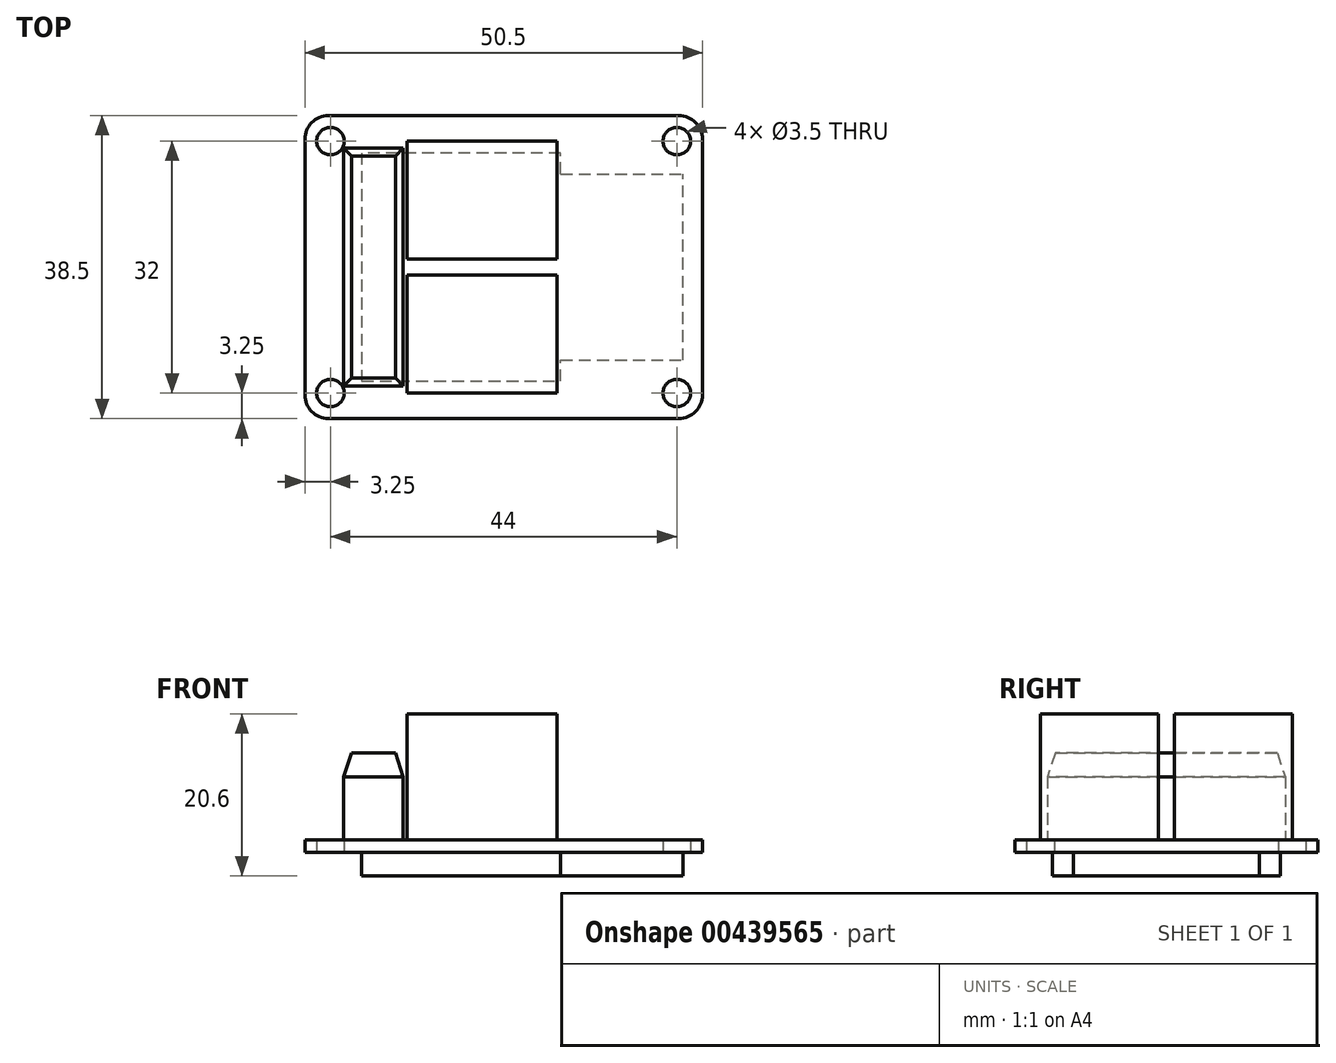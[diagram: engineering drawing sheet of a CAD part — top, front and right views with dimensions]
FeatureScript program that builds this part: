
annotation { "Feature Type Name" : "Feature", "Feature Type Description" : "" }
export const myFeature = defineFeature(function(context is Context, id is Id, definition is map)
    precondition{}
    {
        {
            var Q0;
            Q0=qCreatedBy(makeId("Top.planeOp"),FACE);
            var sketch = newSketch(context, id + "F0", { "sketchPlane" : qUnion([Q0])});
            skLineSegment(sketch, "E0.bottom", {"start": v(-28, -60) * mm, "end": v(22.5, -60) * mm});
            skLineSegment(sketch, "E0.top", {"start": v(-28, -98.5) * mm, "end": v(22.5, -98.5) * mm});
            skLineSegment(sketch, "E0.left", {"start": v(-28, -60) * mm, "end": v(-28, -98.5) * mm});
            skLineSegment(sketch, "E0.right", {"start": v(22.5, -60) * mm, "end": v(22.5, -98.5) * mm});
            skCircle(sketch, "E1", {"center": v(-24.75, -63.25) * mm, "radius": 1.75 * mm});
            skCircle(sketch, "E2.0.1.0", {"center": v(-24.75, -95.25) * mm, "radius": 1.75 * mm});
            skCircle(sketch, "E2.1.0.0", {"center": v(19.25, -63.25) * mm, "radius": 1.75 * mm});
            skCircle(sketch, "E2.1.1.0", {"center": v(19.25, -95.25) * mm, "radius": 1.75 * mm});
            skLineSegment(sketch, "E2.direction1", {"start": v(-24.75, -63.25) * mm, "end": v(19.25, -63.25) * mm, "construction": true});
            skLineSegment(sketch, "E2.direction2", {"start": v(-24.75, -63.25) * mm, "end": v(-24.75, -95.25) * mm, "construction": true});
            skSolve(sketch);
        }
        {
            var Q0;
            Q0=makeQuery(id+"F0.imprint","IMPRINT",FACE,{"disambiguationData":[TD([[makeQuery(id+"F0.imprint","IMPRINT",EDGE,{"derivedFrom":sQuery(id+"F0.wireOp",EDGE,"E0.bottom")}),-1.0]])]});
            extrude(context, id + "F1", {"entities" : qUnion([Q0]), "depth" : 4.6 * mm, "hasSecondDirection" : true, "secondDirectionOppositeDirection" : false, "secondDirectionDepth" : 3 * mm});
        }
        {
            var Q0;
            Q0=makeQuery(id+"F1.opExtrude","SWEPT_EDGE",EDGE,{"disambiguationData":[OSD([sQuery(id+"F0.wireOp",EDGE,"E0.top"),sQuery(id+"F0.wireOp",EDGE,"E0.right")])]});
            var Q1;
            Q1=makeQuery(id+"F1.opExtrude","SWEPT_EDGE",EDGE,{"disambiguationData":[OSD([sQuery(id+"F0.wireOp",EDGE,"E0.bottom"),sQuery(id+"F0.wireOp",EDGE,"E0.right")])]});
            var Q2;
            Q2=makeQuery(id+"F1.opExtrude","SWEPT_EDGE",EDGE,{"disambiguationData":[OSD([sQuery(id+"F0.wireOp",EDGE,"E0.bottom"),sQuery(id+"F0.wireOp",EDGE,"E0.left")])]});
            var Q3;
            Q3=makeQuery(id+"F1.opExtrude","SWEPT_EDGE",EDGE,{"disambiguationData":[OSD([sQuery(id+"F0.wireOp",EDGE,"E0.top"),sQuery(id+"F0.wireOp",EDGE,"E0.left")])]});
            fillet(context, id + "F2", {"entities" : qUnion([Q0, Q1, Q2, Q3]), "radius" : 3 * mm, "tangentPropagation" : true, "allowEdgeOverflow" : false});
        }
        {
            var Q0;
            Q0=makeQuery(id+"F1.opExtrude","CAP_FACE",FACE,{"disambiguationData":[OSD([sQuery(id+"F0.wireOp",EDGE,"E0.bottom"),sQuery(id+"F0.wireOp",EDGE,"E0.top"),sQuery(id+"F0.wireOp",EDGE,"E0.left"),sQuery(id+"F0.wireOp",EDGE,"E0.right"),sQuery(id+"F0.wireOp",EDGE,"E1"),sQuery(id+"F0.wireOp",EDGE,"E2.0.1.0"),sQuery(id+"F0.wireOp",EDGE,"E2.1.0.0"),sQuery(id+"F0.wireOp",EDGE,"E2.1.1.0")])],"isStart":true});
            var sketch = newSketch(context, id + "F3", { "sketchPlane" : qUnion([Q0])});
            skLineSegment(sketch, "E3.0.0", {"start": v(19.5, 98.5) * mm, "end": v(-25, 98.5) * mm, "construction": true});
            skArc(sketch, "E3.0.1", {"start": v(-25, 98.5) * mm, "mid": v(-27.12, 97.62) * mm, "end": v(-28, 95.5) * mm, "construction": true});
            skLineSegment(sketch, "E3.0.2", {"start": v(-28, 95.5) * mm, "end": v(-28, 63) * mm, "construction": true});
            skArc(sketch, "E3.0.3", {"start": v(-28, 63) * mm, "mid": v(-27.12, 60.88) * mm, "end": v(-25, 60) * mm, "construction": true});
            skLineSegment(sketch, "E3.0.4", {"start": v(-25, 60) * mm, "end": v(19.5, 60) * mm, "construction": true});
            skArc(sketch, "E3.0.5", {"start": v(19.5, 60) * mm, "mid": v(21.62, 60.88) * mm, "end": v(22.5, 63) * mm, "construction": true});
            skLineSegment(sketch, "E3.0.6", {"start": v(22.5, 63) * mm, "end": v(22.5, 95.5) * mm, "construction": true});
            skArc(sketch, "E3.0.7", {"start": v(22.5, 95.5) * mm, "mid": v(21.62, 97.62) * mm, "end": v(19.5, 98.5) * mm, "construction": true});
            skCircle(sketch, "E4.0", {"center": v(-24.75, 95.25) * mm, "radius": 1.75 * mm, "construction": true});
            skCircle(sketch, "E5.0", {"center": v(19.25, 95.25) * mm, "radius": 1.75 * mm, "construction": true});
            skCircle(sketch, "E6.0", {"center": v(19.25, 63.25) * mm, "radius": 1.75 * mm, "construction": true});
            skCircle(sketch, "E7.0", {"center": v(-24.75, 63.25) * mm, "radius": 1.75 * mm, "construction": true});
            skLineSegment(sketch, "E8", {"start": v(-20.77, 64.75) * mm, "end": v(-20.77, 93.75) * mm});
            skLineSegment(sketch, "E9", {"start": v(-20.77, 93.75) * mm, "end": v(4.5, 93.75) * mm});
            skLineSegment(sketch, "E10", {"start": v(4.5, 93.75) * mm, "end": v(4.5, 64.75) * mm});
            skLineSegment(sketch, "E11", {"start": v(4.5, 64.75) * mm, "end": v(-20.77, 64.75) * mm});
            skPoint(sketch, "E12.orphan", {"position": v(19.25, 93.75) * mm});
            skLineSegment(sketch, "E13.bottom", {"start": v(4.5, 91.07) * mm, "end": v(20, 91.07) * mm});
            skLineSegment(sketch, "E13.top", {"start": v(4.5, 67.43) * mm, "end": v(20, 67.43) * mm});
            skLineSegment(sketch, "E13.left", {"start": v(4.5, 91.07) * mm, "end": v(4.5, 67.43) * mm});
            skLineSegment(sketch, "E13.right", {"start": v(20, 91.07) * mm, "end": v(20, 67.43) * mm});
            skSolve(sketch);
        }
        {
            var Q0;
            Q0=makeQuery(id+"F3.imprint","IMPRINT",FACE,{"disambiguationData":[TD([[makeQuery(id+"F3.imprint","IMPRINT",EDGE,{"derivedFrom":sQuery(id+"F3.wireOp",EDGE,"E8")}),-1.0]])]});
            var Q1;
            Q1=makeQuery(id+"F3.imprint","IMPRINT",FACE,{"disambiguationData":[TD([[makeQuery(id+"F3.imprint","IMPRINT",EDGE,{"derivedFrom":sQuery(id+"F3.wireOp",EDGE,"E13.bottom")}),-1.0]])]});
            extrude(context, id + "F4", {"entities" : qUnion([Q0, Q1]), "operationType" : NewBodyOperationType.ADD, "depth" : 3 * mm});
        }
        {
            var Q0;
            Q0=makeQuery(id+"F1.opExtrude","CAP_FACE",FACE,{"disambiguationData":[OSD([sQuery(id+"F0.wireOp",EDGE,"E0.bottom"),sQuery(id+"F0.wireOp",EDGE,"E0.top"),sQuery(id+"F0.wireOp",EDGE,"E0.left"),sQuery(id+"F0.wireOp",EDGE,"E0.right"),sQuery(id+"F0.wireOp",EDGE,"E1"),sQuery(id+"F0.wireOp",EDGE,"E2.0.1.0"),sQuery(id+"F0.wireOp",EDGE,"E2.1.0.0"),sQuery(id+"F0.wireOp",EDGE,"E2.1.1.0")])],"isStart":false});
            var sketch = newSketch(context, id + "F5", { "sketchPlane" : qUnion([Q0])});
            skLineSegment(sketch, "E14.0.0", {"start": v(-28, -63) * mm, "end": v(-28, -95.5) * mm, "construction": true});
            skArc(sketch, "E14.0.1", {"start": v(-28, -95.5) * mm, "mid": v(-27.12, -97.62) * mm, "end": v(-25, -98.5) * mm, "construction": true});
            skLineSegment(sketch, "E14.0.2", {"start": v(-25, -98.5) * mm, "end": v(19.5, -98.5) * mm, "construction": true});
            skArc(sketch, "E14.0.3", {"start": v(19.5, -98.5) * mm, "mid": v(21.62, -97.62) * mm, "end": v(22.5, -95.5) * mm, "construction": true});
            skLineSegment(sketch, "E14.0.4", {"start": v(22.5, -95.5) * mm, "end": v(22.5, -63) * mm, "construction": true});
            skArc(sketch, "E14.0.5", {"start": v(22.5, -63) * mm, "mid": v(21.62, -60.88) * mm, "end": v(19.5, -60) * mm, "construction": true});
            skLineSegment(sketch, "E14.0.6", {"start": v(19.5, -60) * mm, "end": v(-25, -60) * mm, "construction": true});
            skArc(sketch, "E14.0.7", {"start": v(-25, -60) * mm, "mid": v(-27.12, -60.88) * mm, "end": v(-28, -63) * mm, "construction": true});
            skLineSegment(sketch, "E15.bottom", {"start": v(4, -63.25) * mm, "end": v(-15, -63.25) * mm});
            skLineSegment(sketch, "E15.top", {"start": v(4, -95.25) * mm, "end": v(-15, -95.25) * mm});
            skLineSegment(sketch, "E15.left", {"start": v(4, -63.25) * mm, "end": v(4, -95.25) * mm});
            skLineSegment(sketch, "E15.right", {"start": v(-15, -63.25) * mm, "end": v(-15, -95.25) * mm});
            skLineSegment(sketch, "E16", {"start": v(22.5, -79.25) * mm, "end": v(-28, -79.25) * mm, "construction": true});
            skPoint(sketch, "E17", {"position": v(4, -79.25) * mm});
            skLineSegment(sketch, "E18", {"start": v(4, -80.25) * mm, "end": v(-15, -80.25) * mm});
            skLineSegment(sketch, "E19.MirrorCS", {"start": v(4, -78.25) * mm, "end": v(-15, -78.25) * mm});
            skLineSegment(sketch, "E20.bottom", {"start": v(-15.5, -64.15) * mm, "end": v(-23.1, -64.15) * mm});
            skLineSegment(sketch, "E20.top", {"start": v(-15.5, -94.35) * mm, "end": v(-23.1, -94.35) * mm});
            skLineSegment(sketch, "E20.left", {"start": v(-15.5, -64.15) * mm, "end": v(-15.5, -94.35) * mm});
            skLineSegment(sketch, "E20.right", {"start": v(-23.1, -64.15) * mm, "end": v(-23.1, -94.35) * mm});
            skPoint(sketch, "E21", {"position": v(-15.5, -79.25) * mm});
            skSolve(sketch);
        }
        {
            var Q0;
            {var subQ0=sQuery(id+"F5.wireOp",EDGE,"E15.bottom");Q0=makeQuery(id+"F5.imprint","IMPRINT",FACE,{"disambiguationData":[TD([[makeQuery(id+"F5.imprint","IMPRINT",EDGE,{"derivedFrom":subQ0}),1.0]])]});}
            var Q1;
            {var subQ0=sQuery(id+"F5.wireOp",EDGE,"E15.top");Q1=makeQuery(id+"F5.imprint","IMPRINT",FACE,{"disambiguationData":[TD([[makeQuery(id+"F5.imprint","IMPRINT",EDGE,{"derivedFrom":subQ0}),-1.0]])]});}
            extrude(context, id + "F6", {"entities" : qUnion([Q0, Q1]), "operationType" : NewBodyOperationType.ADD, "depth" : 16 * mm});
        }
        {
            var Q0;
            Q0=makeQuery(id+"F5.imprint","IMPRINT",FACE,{"disambiguationData":[TD([[makeQuery(id+"F5.imprint","IMPRINT",EDGE,{"derivedFrom":sQuery(id+"F5.wireOp",EDGE,"E20.bottom")}),1.0]])]});
            extrude(context, id + "F7", {"entities" : qUnion([Q0]), "operationType" : NewBodyOperationType.ADD, "depth" : 11 * mm});
        }
        {
            var Q0;
            Q0=makeQuery(id+"F7.opExtrude","CAP_EDGE",EDGE,{"disambiguationData":[OSD([sQuery(id+"F5.wireOp",EDGE,"E20.right")])],"isStart":false});
            var Q1;
            Q1=makeQuery(id+"F7.opExtrude","CAP_EDGE",EDGE,{"disambiguationData":[OSD([sQuery(id+"F5.wireOp",EDGE,"E20.bottom")])],"isStart":false});
            var Q2;
            Q2=makeQuery(id+"F7.opExtrude","CAP_EDGE",EDGE,{"disambiguationData":[OSD([sQuery(id+"F5.wireOp",EDGE,"E20.top")])],"isStart":false});
            var Q3;
            Q3=makeQuery(id+"F7.opExtrude","CAP_EDGE",EDGE,{"disambiguationData":[OSD([sQuery(id+"F5.wireOp",EDGE,"E20.left")])],"isStart":false});
            chamfer(context, id + "F8", {"entities" : qUnion([Q0, Q1, Q2, Q3]), "chamferType" : ChamferType.TWO_OFFSETS, "width1" : 1 * mm, "oppositeDirection" : false, "width2" : 3 * mm, "tangentPropagation" : true});
        }
    });
